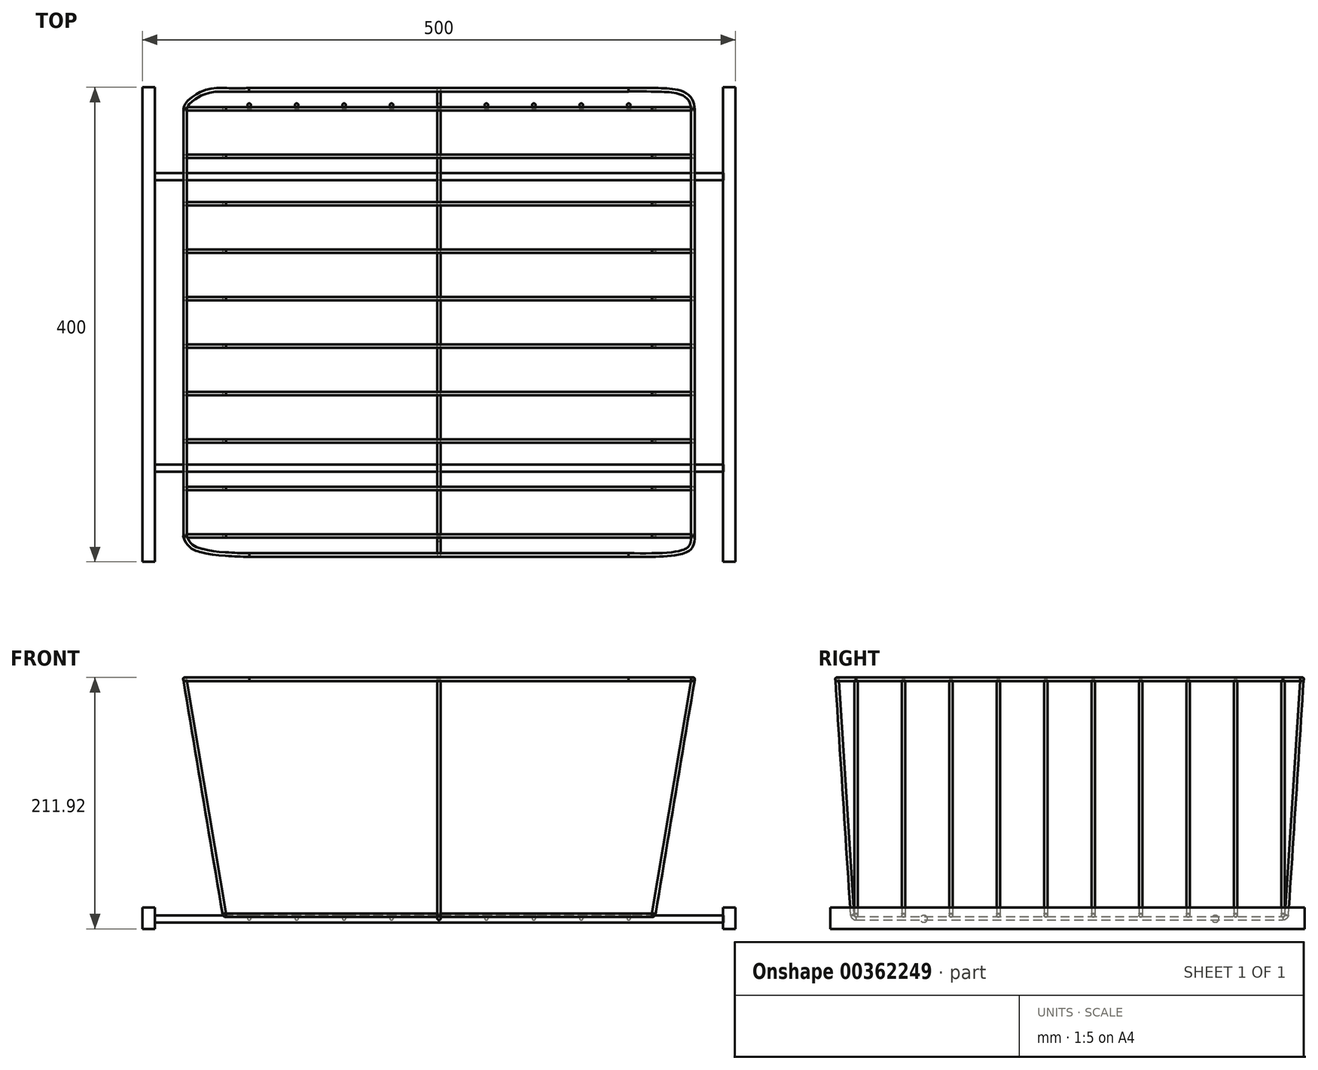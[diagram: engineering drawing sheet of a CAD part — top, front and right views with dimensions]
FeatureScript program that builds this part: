
annotation { "Feature Type Name" : "Feature", "Feature Type Description" : "" }
export const myFeature = defineFeature(function(context is Context, id is Id, definition is map)
    precondition{}
    {
        {
            var Q0;
            Q0=qCreatedBy(makeId("Front.planeOp"),FACE);
            var sketch = newSketch(context, id + "F0", { "sketchPlane" : qUnion([Q0])});
            skLineSegment(sketch, "E0.bottom", {"start": v(-179.58, 0) * mm, "end": v(180.42, 0) * mm});
            skLineSegment(sketch, "E0.top", {"start": v(-179.58, -1.5) * mm, "end": v(180.42, -1.5) * mm});
            skLineSegment(sketch, "E0.left", {"start": v(-179.58, 0) * mm, "end": v(-179.58, -1.5) * mm});
            skLineSegment(sketch, "E0.right", {"start": v(180.42, 0) * mm, "end": v(180.42, -1.5) * mm});
            skSolve(sketch);
        }
        {
            var Q0;
            Q0=makeQuery(id+"F0.imprint","IMPRINT",FACE,{"disambiguationData":[TD([[makeQuery(id+"F0.imprint","IMPRINT",EDGE,{"derivedFrom":sQuery(id+"F0.wireOp",EDGE,"E0.bottom")}),-1.0]])]});
            var Q1;
            Q1=sQuery(id+"F0.wireOp",EDGE,"E0.bottom");
            revolve(context, id + "F1", {"entities" : qUnion([Q0]), "axis" : qUnion([Q1]), "revolveType" : RevolveType.FULL});
        }
        {
            var Q0;
            Q0=qCreatedBy(makeId("Front.planeOp"),FACE);
            var sketch = newSketch(context, id + "F2", { "sketchPlane" : qUnion([Q0])});
            skLineSegment(sketch, "E1", {"start": v(-179.62, 1.46) * mm, "end": v(-212.66, 198.71) * mm});
            skLineSegment(sketch, "E2", {"start": v(-212.66, 198.71) * mm, "end": v(-214.16, 198.71) * mm});
            skLineSegment(sketch, "E3", {"start": v(-181.12, 1.46) * mm, "end": v(-179.62, 1.46) * mm});
            skLineSegment(sketch, "E4", {"start": v(-181.12, 1.46) * mm, "end": v(-214.16, 198.71) * mm});
            skSolve(sketch);
        }
        {
            var Q0;
            Q0 = qSketchRegion(id + "F2", true);
            var Q1;
            Q1=sQuery(id+"F2.wireOp",EDGE,"E4");
            revolve(context, id + "F3", {"entities" : qUnion([Q0]), "axis" : qUnion([Q1]), "revolveType" : RevolveType.FULL});
        }
        {
            var Q0;
            Q0=qCreatedBy(makeId("Front.planeOp"),FACE);
            var sketch = newSketch(context, id + "F4", { "sketchPlane" : qUnion([Q0])});
            skFitSpline(sketch, "E5", {"points": [v(-182.54, 1) * mm, v(-182.18, 0.12) * mm, v(-180.93, -1.14) * mm, v(-179.6, -1.47) * mm], "startDerivative": vector(0.9, -2.93) * mm, "endDerivative": vector(4, -0.37) * mm});
            skSolve(sketch);
        }
        {
            var Q0;
            Q0=makeQuery(id+"F1.opRevolve","SWEPT_FACE",FACE,{"disambiguationData":[OSD([sQuery(id+"F0.wireOp",EDGE,"E0.left")])]});
            var Q1;
            Q1=sQuery(id+"F4.wireOp",EDGE,"E5");
            sweep(context, id + "F5", {"profiles" : qUnion([Q0]), "path" : qUnion([Q1])});
        }
        {
            var Q0;
            Q0=makeQuery(id+"F3.opRevolve","SWEPT_BODY",BODY,{"disambiguationData":[OSD([sQuery(id+"F2.wireOp",EDGE,"E1"),sQuery(id+"F2.wireOp",EDGE,"E2"),sQuery(id+"F2.wireOp",EDGE,"E3"),sQuery(id+"F2.wireOp",EDGE,"E4")])]});
            var Q1;
            Q1=makeQuery(id+"F5.opSweep","SWEPT_BODY",BODY,{"disambiguationData":[OSD([sQuery(id+"F0.wireOp",EDGE,"E0.left"),sQuery(id+"F4.wireOp",EDGE,"E5")])]});
            var Q2;
            Q2=qCreatedBy(makeId("Right.planeOp"),FACE);
            mirror(context, id + "F6", {"operationType" : NewBodyOperationType.ADD, "entities" : qUnion([Q0, Q1]), "mirrorPlane" : qUnion([Q2])});
        }
        {
            var Q0;
            Q0=makeQuery(id+"F1.opRevolve","SWEPT_BODY",BODY,{"disambiguationData":[OSD([sQuery(id+"F0.wireOp",EDGE,"E0.bottom"),sQuery(id+"F0.wireOp",EDGE,"E0.top"),sQuery(id+"F0.wireOp",EDGE,"E0.left"),sQuery(id+"F0.wireOp",EDGE,"E0.right")])]});
            transform(context, id + "F7", {"entities" : qUnion([Q0]), "transformType" : TransformType.TRANSLATION_3D, "dx" : 0 * mm, "dy" : 40 * mm, "dz" : 0 * mm, "makeCopy" : true});
        }
        {
            var Q0;
            Q0=makeQuery(id+"F7.opPattern","COPY",BODY,{"derivedFrom":makeQuery(id+"F1.opRevolve","SWEPT_BODY",BODY,{"disambiguationData":[OSD([sQuery(id+"F0.wireOp",EDGE,"E0.bottom"),sQuery(id+"F0.wireOp",EDGE,"E0.top"),sQuery(id+"F0.wireOp",EDGE,"E0.left"),sQuery(id+"F0.wireOp",EDGE,"E0.right")])]}),"instanceName":"1"});
            transform(context, id + "F8", {"entities" : qUnion([Q0]), "transformType" : TransformType.TRANSLATION_3D, "dx" : 0 * mm, "dy" : 40 * mm, "dz" : 0 * mm, "makeCopy" : true});
        }
        {
            var Q0;
            Q0=makeQuery(id+"F8.opPattern","COPY",BODY,{"derivedFrom":makeQuery(id+"F7.opPattern","COPY",BODY,{"derivedFrom":makeQuery(id+"F1.opRevolve","SWEPT_BODY",BODY,{"disambiguationData":[OSD([sQuery(id+"F0.wireOp",EDGE,"E0.bottom"),sQuery(id+"F0.wireOp",EDGE,"E0.top"),sQuery(id+"F0.wireOp",EDGE,"E0.left"),sQuery(id+"F0.wireOp",EDGE,"E0.right")])]}),"instanceName":"1"}),"instanceName":"1"});
            transform(context, id + "F9", {"entities" : qUnion([Q0]), "transformType" : TransformType.TRANSLATION_3D, "dx" : 0 * mm, "dy" : 40 * mm, "dz" : 0 * mm, "makeCopy" : true});
        }
        {
            var Q0;
            Q0=makeQuery(id+"F9.opPattern","COPY",BODY,{"derivedFrom":makeQuery(id+"F8.opPattern","COPY",BODY,{"derivedFrom":makeQuery(id+"F7.opPattern","COPY",BODY,{"derivedFrom":makeQuery(id+"F1.opRevolve","SWEPT_BODY",BODY,{"disambiguationData":[OSD([sQuery(id+"F0.wireOp",EDGE,"E0.bottom"),sQuery(id+"F0.wireOp",EDGE,"E0.top"),sQuery(id+"F0.wireOp",EDGE,"E0.left"),sQuery(id+"F0.wireOp",EDGE,"E0.right")])]}),"instanceName":"1"}),"instanceName":"1"}),"instanceName":"1"});
            transform(context, id + "F10", {"entities" : qUnion([Q0]), "transformType" : TransformType.TRANSLATION_3D, "dx" : 0 * mm, "dy" : 40 * mm, "dz" : 0 * mm, "makeCopy" : true});
        }
        {
            var Q0;
            Q0=makeQuery(id+"F10.opPattern","COPY",BODY,{"derivedFrom":makeQuery(id+"F9.opPattern","COPY",BODY,{"derivedFrom":makeQuery(id+"F8.opPattern","COPY",BODY,{"derivedFrom":makeQuery(id+"F7.opPattern","COPY",BODY,{"derivedFrom":makeQuery(id+"F1.opRevolve","SWEPT_BODY",BODY,{"disambiguationData":[OSD([sQuery(id+"F0.wireOp",EDGE,"E0.bottom"),sQuery(id+"F0.wireOp",EDGE,"E0.top"),sQuery(id+"F0.wireOp",EDGE,"E0.left"),sQuery(id+"F0.wireOp",EDGE,"E0.right")])]}),"instanceName":"1"}),"instanceName":"1"}),"instanceName":"1"}),"instanceName":"1"});
            transform(context, id + "F11", {"entities" : qUnion([Q0]), "transformType" : TransformType.TRANSLATION_3D, "dx" : 0 * mm, "dy" : 40 * mm, "dz" : 0 * mm, "makeCopy" : true});
        }
        {
            var Q0;
            Q0=makeQuery(id+"F11.opPattern","COPY",BODY,{"derivedFrom":makeQuery(id+"F10.opPattern","COPY",BODY,{"derivedFrom":makeQuery(id+"F9.opPattern","COPY",BODY,{"derivedFrom":makeQuery(id+"F8.opPattern","COPY",BODY,{"derivedFrom":makeQuery(id+"F7.opPattern","COPY",BODY,{"derivedFrom":makeQuery(id+"F1.opRevolve","SWEPT_BODY",BODY,{"disambiguationData":[OSD([sQuery(id+"F0.wireOp",EDGE,"E0.bottom"),sQuery(id+"F0.wireOp",EDGE,"E0.top"),sQuery(id+"F0.wireOp",EDGE,"E0.left"),sQuery(id+"F0.wireOp",EDGE,"E0.right")])]}),"instanceName":"1"}),"instanceName":"1"}),"instanceName":"1"}),"instanceName":"1"}),"instanceName":"1"});
            transform(context, id + "F12", {"entities" : qUnion([Q0]), "transformType" : TransformType.TRANSLATION_3D, "dx" : 0 * mm, "dy" : 40 * mm, "dz" : 0 * mm, "makeCopy" : true});
        }
        {
            var Q0;
            Q0=makeQuery(id+"F12.opPattern","COPY",BODY,{"derivedFrom":makeQuery(id+"F11.opPattern","COPY",BODY,{"derivedFrom":makeQuery(id+"F10.opPattern","COPY",BODY,{"derivedFrom":makeQuery(id+"F9.opPattern","COPY",BODY,{"derivedFrom":makeQuery(id+"F8.opPattern","COPY",BODY,{"derivedFrom":makeQuery(id+"F7.opPattern","COPY",BODY,{"derivedFrom":makeQuery(id+"F1.opRevolve","SWEPT_BODY",BODY,{"disambiguationData":[OSD([sQuery(id+"F0.wireOp",EDGE,"E0.bottom"),sQuery(id+"F0.wireOp",EDGE,"E0.top"),sQuery(id+"F0.wireOp",EDGE,"E0.left"),sQuery(id+"F0.wireOp",EDGE,"E0.right")])]}),"instanceName":"1"}),"instanceName":"1"}),"instanceName":"1"}),"instanceName":"1"}),"instanceName":"1"}),"instanceName":"1"});
            transform(context, id + "F13", {"entities" : qUnion([Q0]), "transformType" : TransformType.TRANSLATION_3D, "dx" : 0 * mm, "dy" : 40 * mm, "dz" : 0 * mm, "makeCopy" : true});
        }
        {
            var Q0;
            Q0=makeQuery(id+"F13.opPattern","COPY",BODY,{"derivedFrom":makeQuery(id+"F12.opPattern","COPY",BODY,{"derivedFrom":makeQuery(id+"F11.opPattern","COPY",BODY,{"derivedFrom":makeQuery(id+"F10.opPattern","COPY",BODY,{"derivedFrom":makeQuery(id+"F9.opPattern","COPY",BODY,{"derivedFrom":makeQuery(id+"F8.opPattern","COPY",BODY,{"derivedFrom":makeQuery(id+"F7.opPattern","COPY",BODY,{"derivedFrom":makeQuery(id+"F1.opRevolve","SWEPT_BODY",BODY,{"disambiguationData":[OSD([sQuery(id+"F0.wireOp",EDGE,"E0.bottom"),sQuery(id+"F0.wireOp",EDGE,"E0.top"),sQuery(id+"F0.wireOp",EDGE,"E0.left"),sQuery(id+"F0.wireOp",EDGE,"E0.right")])]}),"instanceName":"1"}),"instanceName":"1"}),"instanceName":"1"}),"instanceName":"1"}),"instanceName":"1"}),"instanceName":"1"}),"instanceName":"1"});
            transform(context, id + "F14", {"entities" : qUnion([Q0]), "transformType" : TransformType.TRANSLATION_3D, "dx" : 0 * mm, "dy" : 40 * mm, "dz" : 0 * mm, "makeCopy" : true});
        }
        {
            var Q0;
            Q0=makeQuery(id+"F14.opPattern","COPY",BODY,{"derivedFrom":makeQuery(id+"F13.opPattern","COPY",BODY,{"derivedFrom":makeQuery(id+"F12.opPattern","COPY",BODY,{"derivedFrom":makeQuery(id+"F11.opPattern","COPY",BODY,{"derivedFrom":makeQuery(id+"F10.opPattern","COPY",BODY,{"derivedFrom":makeQuery(id+"F9.opPattern","COPY",BODY,{"derivedFrom":makeQuery(id+"F8.opPattern","COPY",BODY,{"derivedFrom":makeQuery(id+"F7.opPattern","COPY",BODY,{"derivedFrom":makeQuery(id+"F1.opRevolve","SWEPT_BODY",BODY,{"disambiguationData":[OSD([sQuery(id+"F0.wireOp",EDGE,"E0.bottom"),sQuery(id+"F0.wireOp",EDGE,"E0.top"),sQuery(id+"F0.wireOp",EDGE,"E0.left"),sQuery(id+"F0.wireOp",EDGE,"E0.right")])]}),"instanceName":"1"}),"instanceName":"1"}),"instanceName":"1"}),"instanceName":"1"}),"instanceName":"1"}),"instanceName":"1"}),"instanceName":"1"}),"instanceName":"1"});
            transform(context, id + "F15", {"entities" : qUnion([Q0]), "transformType" : TransformType.TRANSLATION_3D, "dx" : 0 * mm, "dy" : 40 * mm, "dz" : 0 * mm, "makeCopy" : true});
        }
        {
            var Q0;
            Q0=qCreatedBy(makeId("Right.planeOp"),FACE);
            var sketch = newSketch(context, id + "F16", { "sketchPlane" : qUnion([Q0])});
            skLineSegment(sketch, "E6.bottom", {"start": v(360, -1.07) * mm, "end": v(0, -1.07) * mm});
            skLineSegment(sketch, "E6.top", {"start": v(360, -2.57) * mm, "end": v(0, -2.57) * mm});
            skLineSegment(sketch, "E6.left", {"start": v(360, -1.07) * mm, "end": v(360, -2.57) * mm});
            skLineSegment(sketch, "E6.right", {"start": v(0, -1.07) * mm, "end": v(0, -2.57) * mm});
            skSolve(sketch);
        }
        {
            var Q0;
            Q0 = qSketchRegion(id + "F16", true);
            var Q1;
            Q1=sQuery(id+"F16.wireOp",EDGE,"E6.top");
            revolve(context, id + "F17", {"entities" : qUnion([Q0]), "axis" : qUnion([Q1]), "revolveType" : RevolveType.FULL});
        }
        {
            var Q0;
            Q0=qCreatedBy(makeId("Right.planeOp"),FACE);
            var sketch = newSketch(context, id + "F18", { "sketchPlane" : qUnion([Q0])});
            skLineSegment(sketch, "E7", {"start": v(-1.6, 0) * mm, "end": v(-14.52, 199.58) * mm});
            skLineSegment(sketch, "E8", {"start": v(-14.52, 199.58) * mm, "end": v(-16.02, 199.58) * mm});
            skLineSegment(sketch, "E9", {"start": v(-16.02, 199.58) * mm, "end": v(-3.1, 0) * mm});
            skLineSegment(sketch, "E10", {"start": v(-3.1, 0) * mm, "end": v(-1.6, 0) * mm});
            skSolve(sketch);
        }
        {
            var Q0;
            Q0 = qSketchRegion(id + "F18", true);
            var Q1;
            Q1=sQuery(id+"F18.wireOp",EDGE,"E9");
            revolve(context, id + "F19", {"entities" : qUnion([Q0]), "axis" : qUnion([Q1]), "revolveType" : RevolveType.FULL});
        }
        {
            var Q0;
            Q0=qCreatedBy(makeId("Right.planeOp"),FACE);
            var sketch = newSketch(context, id + "F20", { "sketchPlane" : qUnion([Q0])});
            skFitSpline(sketch, "E11", {"points": [v(-4.59, -0.18) * mm, v(-3.92, -1.73) * mm, v(-1.93, -3.55) * mm, v(0, -4.03) * mm], "startDerivative": vector(1.58, -5.04) * mm, "endDerivative": vector(5.92, -0.67) * mm});
            skSolve(sketch);
        }
        {
            var Q0;
            Q0=makeQuery(id+"F17.opRevolve","SWEPT_FACE",FACE,{"disambiguationData":[OSD([sQuery(id+"F16.wireOp",EDGE,"E6.right")])]});
            var Q1;
            Q1=sQuery(id+"F20.wireOp",EDGE,"E11");
            sweep(context, id + "F21", {"profiles" : qUnion([Q0]), "path" : qUnion([Q1])});
        }
        {
            var Q0;
            Q0=qCreatedBy(makeId("Front.planeOp"),FACE);
            cPlane(context, id + "F22", {"entities" : qUnion([Q0]), "cplaneType" : CPlaneType.OFFSET, "offset" : 180 * mm, "oppositeDirection" : true, "width" : 150 * mm, "height" : 150 * mm});
        }
        {
            var Q0;
            Q0=makeQuery(id+"F19.opRevolve","SWEPT_BODY",BODY,{"disambiguationData":[OSD([sQuery(id+"F18.wireOp",EDGE,"E7"),sQuery(id+"F18.wireOp",EDGE,"E8"),sQuery(id+"F18.wireOp",EDGE,"E9"),sQuery(id+"F18.wireOp",EDGE,"E10")])]});
            var Q1;
            Q1=makeQuery(id+"F21.opSweep","SWEPT_BODY",BODY,{"disambiguationData":[OSD([sQuery(id+"F16.wireOp",EDGE,"E6.right"),sQuery(id+"F20.wireOp",EDGE,"E11")])]});
            var Q2;
            Q2=qCreatedBy(id+"F22.planeOp",FACE);
            mirror(context, id + "F23", {"entities" : qUnion([Q0, Q1]), "mirrorPlane" : qUnion([Q2])});
        }
        {
            var Q0;
            Q0=makeQuery(id+"F23.opPattern","COPY",BODY,{"derivedFrom":makeQuery(id+"F21.opSweep","SWEPT_BODY",BODY,{"disambiguationData":[OSD([sQuery(id+"F16.wireOp",EDGE,"E6.right"),sQuery(id+"F20.wireOp",EDGE,"E11")])]}),"instanceName":"1"});
            transform(context, id + "F24", {"entities" : qUnion([Q0]), "transformType" : TransformType.TRANSLATION_3D, "dx" : 40 * mm, "dy" : 0 * mm, "dz" : 0 * mm, "makeCopy" : true});
        }
        {
            var Q0;
            Q0=makeQuery(id+"F24.opPattern","COPY",BODY,{"derivedFrom":makeQuery(id+"F23.opPattern","COPY",BODY,{"derivedFrom":makeQuery(id+"F21.opSweep","SWEPT_BODY",BODY,{"disambiguationData":[OSD([sQuery(id+"F16.wireOp",EDGE,"E6.right"),sQuery(id+"F20.wireOp",EDGE,"E11")])]}),"instanceName":"1"}),"instanceName":"1"});
            transform(context, id + "F25", {"entities" : qUnion([Q0]), "transformType" : TransformType.TRANSLATION_3D, "dx" : 40 * mm, "dy" : 0 * mm, "dz" : 0 * mm, "makeCopy" : true});
        }
        {
            var Q0;
            Q0=makeQuery(id+"F25.opPattern","COPY",BODY,{"derivedFrom":makeQuery(id+"F24.opPattern","COPY",BODY,{"derivedFrom":makeQuery(id+"F23.opPattern","COPY",BODY,{"derivedFrom":makeQuery(id+"F21.opSweep","SWEPT_BODY",BODY,{"disambiguationData":[OSD([sQuery(id+"F16.wireOp",EDGE,"E6.right"),sQuery(id+"F20.wireOp",EDGE,"E11")])]}),"instanceName":"1"}),"instanceName":"1"}),"instanceName":"1"});
            transform(context, id + "F26", {"entities" : qUnion([Q0]), "transformType" : TransformType.TRANSLATION_3D, "dx" : 40 * mm, "dy" : 0 * mm, "dz" : 0 * mm, "makeCopy" : true});
        }
        {
            var Q0;
            Q0=makeQuery(id+"F26.opPattern","COPY",BODY,{"derivedFrom":makeQuery(id+"F25.opPattern","COPY",BODY,{"derivedFrom":makeQuery(id+"F24.opPattern","COPY",BODY,{"derivedFrom":makeQuery(id+"F23.opPattern","COPY",BODY,{"derivedFrom":makeQuery(id+"F21.opSweep","SWEPT_BODY",BODY,{"disambiguationData":[OSD([sQuery(id+"F16.wireOp",EDGE,"E6.right"),sQuery(id+"F20.wireOp",EDGE,"E11")])]}),"instanceName":"1"}),"instanceName":"1"}),"instanceName":"1"}),"instanceName":"1"});
            transform(context, id + "F27", {"entities" : qUnion([Q0]), "transformType" : TransformType.TRANSLATION_3D, "dx" : 40 * mm, "dy" : 0 * mm, "dz" : 0 * mm, "makeCopy" : true});
        }
        {
            var Q0;
            Q0=makeQuery(id+"F23.opPattern","COPY",BODY,{"derivedFrom":makeQuery(id+"F21.opSweep","SWEPT_BODY",BODY,{"disambiguationData":[OSD([sQuery(id+"F16.wireOp",EDGE,"E6.right"),sQuery(id+"F20.wireOp",EDGE,"E11")])]}),"instanceName":"1"});
            transform(context, id + "F28", {"entities" : qUnion([Q0]), "transformType" : TransformType.TRANSLATION_3D, "dx" : -40 * mm, "dy" : 0 * mm, "dz" : 0 * mm, "makeCopy" : true});
        }
        {
            var Q0;
            Q0=makeQuery(id+"F28.opPattern","COPY",BODY,{"derivedFrom":makeQuery(id+"F23.opPattern","COPY",BODY,{"derivedFrom":makeQuery(id+"F21.opSweep","SWEPT_BODY",BODY,{"disambiguationData":[OSD([sQuery(id+"F16.wireOp",EDGE,"E6.right"),sQuery(id+"F20.wireOp",EDGE,"E11")])]}),"instanceName":"1"}),"instanceName":"1"});
            transform(context, id + "F29", {"entities" : qUnion([Q0]), "transformType" : TransformType.TRANSLATION_3D, "dx" : -40 * mm, "dy" : 0 * mm, "dz" : 0 * mm, "makeCopy" : true});
        }
        {
            var Q0;
            Q0=makeQuery(id+"F29.opPattern","COPY",BODY,{"derivedFrom":makeQuery(id+"F28.opPattern","COPY",BODY,{"derivedFrom":makeQuery(id+"F23.opPattern","COPY",BODY,{"derivedFrom":makeQuery(id+"F21.opSweep","SWEPT_BODY",BODY,{"disambiguationData":[OSD([sQuery(id+"F16.wireOp",EDGE,"E6.right"),sQuery(id+"F20.wireOp",EDGE,"E11")])]}),"instanceName":"1"}),"instanceName":"1"}),"instanceName":"1"});
            transform(context, id + "F30", {"entities" : qUnion([Q0]), "transformType" : TransformType.TRANSLATION_3D, "dx" : -40 * mm, "dy" : 0 * mm, "dz" : 0 * mm, "makeCopy" : true});
        }
        {
            var Q0;
            Q0=makeQuery(id+"F30.opPattern","COPY",BODY,{"derivedFrom":makeQuery(id+"F29.opPattern","COPY",BODY,{"derivedFrom":makeQuery(id+"F28.opPattern","COPY",BODY,{"derivedFrom":makeQuery(id+"F23.opPattern","COPY",BODY,{"derivedFrom":makeQuery(id+"F21.opSweep","SWEPT_BODY",BODY,{"disambiguationData":[OSD([sQuery(id+"F16.wireOp",EDGE,"E6.right"),sQuery(id+"F20.wireOp",EDGE,"E11")])]}),"instanceName":"1"}),"instanceName":"1"}),"instanceName":"1"}),"instanceName":"1"});
            transform(context, id + "F31", {"entities" : qUnion([Q0]), "transformType" : TransformType.TRANSLATION_3D, "dx" : -40 * mm, "dy" : 0 * mm, "dz" : 0 * mm, "makeCopy" : true});
        }
        {
            var Q0;
            Q0=qCreatedBy(makeId("Top.planeOp"),FACE);
            cPlane(context, id + "F32", {"entities" : qUnion([Q0]), "cplaneType" : CPlaneType.OFFSET, "offset" : 199 * mm, "width" : 150 * mm, "height" : 150 * mm});
        }
        {
            var Q0;
            Q0=qCreatedBy(id+"F32.planeOp",FACE);
            var sketch = newSketch(context, id + "F33", { "sketchPlane" : qUnion([Q0])});
            skLineSegment(sketch, "E12.bottom", {"start": v(-160.03, -16.04) * mm, "end": v(159.97, -16.04) * mm});
            skLineSegment(sketch, "E12.top", {"start": v(-160.03, -17.54) * mm, "end": v(159.97, -17.54) * mm});
            skLineSegment(sketch, "E12.left", {"start": v(-160.03, -16.04) * mm, "end": v(-160.03, -17.54) * mm});
            skLineSegment(sketch, "E12.right", {"start": v(159.97, -16.04) * mm, "end": v(159.97, -17.54) * mm});
            skSolve(sketch);
        }
        {
            var Q0;
            Q0=makeQuery(id+"F33.imprint","IMPRINT",FACE,{"disambiguationData":[TD([[makeQuery(id+"F33.imprint","IMPRINT",EDGE,{"derivedFrom":sQuery(id+"F33.wireOp",EDGE,"E12.bottom")}),-1.0]])]});
            var Q1;
            Q1=sQuery(id+"F33.wireOp",EDGE,"E12.bottom");
            revolve(context, id + "F34", {"entities" : qUnion([Q0]), "axis" : qUnion([Q1]), "revolveType" : RevolveType.FULL});
        }
        {
            var Q0;
            Q0=qCreatedBy(id+"F32.planeOp",FACE);
            var sketch = newSketch(context, id + "F35", { "sketchPlane" : qUnion([Q0])});
            skLineSegment(sketch, "E13.bottom", {"start": v(-160.06, 376.04) * mm, "end": v(159.94, 376.04) * mm});
            skLineSegment(sketch, "E13.top", {"start": v(-160.06, 377.54) * mm, "end": v(159.94, 377.54) * mm});
            skLineSegment(sketch, "E13.left", {"start": v(-160.06, 376.04) * mm, "end": v(-160.06, 377.54) * mm});
            skLineSegment(sketch, "E13.right", {"start": v(159.94, 376.04) * mm, "end": v(159.94, 377.54) * mm});
            skSolve(sketch);
        }
        {
            var Q0;
            Q0 = qSketchRegion(id + "F35", true);
            var Q1;
            Q1=sQuery(id+"F35.wireOp",EDGE,"E13.bottom");
            revolve(context, id + "F36", {"entities" : qUnion([Q0]), "axis" : qUnion([Q1]), "revolveType" : RevolveType.FULL});
        }
        {
            var Q0;
            Q0=qCreatedBy(id+"F32.planeOp",FACE);
            var sketch = newSketch(context, id + "F37", { "sketchPlane" : qUnion([Q0])});
            skLineSegment(sketch, "E14.bottom", {"start": v(-215.6, 360) * mm, "end": v(-214.1, 360) * mm});
            skLineSegment(sketch, "E14.top", {"start": v(-215.6, 0) * mm, "end": v(-214.1, 0) * mm});
            skLineSegment(sketch, "E14.left", {"start": v(-215.6, 360) * mm, "end": v(-215.6, 0) * mm});
            skLineSegment(sketch, "E14.right", {"start": v(-214.1, 360) * mm, "end": v(-214.1, 0) * mm});
            skSolve(sketch);
        }
        {
            var Q0;
            Q0 = qSketchRegion(id + "F37", true);
            var Q1;
            Q1=sQuery(id+"F37.wireOp",EDGE,"E14.right");
            revolve(context, id + "F38", {"entities" : qUnion([Q0]), "axis" : qUnion([Q1]), "revolveType" : RevolveType.FULL});
        }
        {
            var Q0;
            Q0=qCreatedBy(id+"F32.planeOp",FACE);
            var sketch = newSketch(context, id + "F39", { "sketchPlane" : qUnion([Q0])});
            skFitSpline(sketch, "E15", {"points": [v(-215.61, 0) * mm, v(-201.65, -13.22) * mm, v(-185.72, -16.08) * mm, v(-159.95, -17.32) * mm], "startDerivative": vector(28.9, -88.62) * mm, "endDerivative": vector(69.27, -0.56) * mm});
            skSolve(sketch);
        }
        {
            var Q0;
            Q0=makeQuery(id+"F34.opRevolve","SWEPT_FACE",FACE,{"disambiguationData":[OSD([sQuery(id+"F33.wireOp",EDGE,"E12.left")])]});
            var Q1;
            Q1=sQuery(id+"F39.wireOp",EDGE,"E15");
            sweep(context, id + "F40", {"profiles" : qUnion([Q0]), "path" : qUnion([Q1])});
        }
        {
            var Q0;
            Q0=qCreatedBy(id+"F32.planeOp",FACE);
            var sketch = newSketch(context, id + "F41", { "sketchPlane" : qUnion([Q0])});
            skFitSpline(sketch, "E16", {"points": [v(-160.14, 377.49) * mm, v(-177.98, 377.45) * mm, v(-198.2, 375.36) * mm, v(-215.39, 360.13) * mm], "startDerivative": vector(-59.47, -0.43) * mm, "endDerivative": vector(-3.54, -51.4) * mm});
            skSolve(sketch);
        }
        {
            var Q0;
            Q0=makeQuery(id+"F36.opRevolve","SWEPT_FACE",FACE,{"disambiguationData":[OSD([sQuery(id+"F35.wireOp",EDGE,"E13.left")])]});
            var Q1;
            Q1=sQuery(id+"F41.wireOp",EDGE,"E16");
            sweep(context, id + "F42", {"profiles" : qUnion([Q0]), "path" : qUnion([Q1])});
        }
        {
            var Q0;
            Q0=qCreatedBy(id+"F32.planeOp",FACE);
            var sketch = newSketch(context, id + "F43", { "sketchPlane" : qUnion([Q0])});
            skLineSegment(sketch, "E17.bottom", {"start": v(214.08, 360) * mm, "end": v(215.58, 360) * mm});
            skLineSegment(sketch, "E17.top", {"start": v(214.08, 0) * mm, "end": v(215.58, 0) * mm});
            skLineSegment(sketch, "E17.left", {"start": v(214.08, 360) * mm, "end": v(214.08, 0) * mm});
            skLineSegment(sketch, "E17.right", {"start": v(215.58, 360) * mm, "end": v(215.58, 0) * mm});
            skSolve(sketch);
        }
        {
            var Q0;
            Q0 = qSketchRegion(id + "F43", true);
            var Q1;
            Q1=sQuery(id+"F43.wireOp",EDGE,"E17.left");
            revolve(context, id + "F44", {"entities" : qUnion([Q0]), "axis" : qUnion([Q1]), "revolveType" : RevolveType.FULL});
        }
        {
            var Q0;
            Q0=qCreatedBy(id+"F32.planeOp",FACE);
            var sketch = newSketch(context, id + "F45", { "sketchPlane" : qUnion([Q0])});
            skFitSpline(sketch, "E18", {"points": [v(159.86, -17.3) * mm, v(193.94, -16.7) * mm, v(210.75, -12.31) * mm, v(215.54, 0) * mm], "startDerivative": vector(59.2, -0.2) * mm, "endDerivative": vector(3.02, 82.73) * mm});
            skSolve(sketch);
        }
        {
            var Q0;
            Q0=makeQuery(id+"F34.opRevolve","SWEPT_FACE",FACE,{"disambiguationData":[OSD([sQuery(id+"F33.wireOp",EDGE,"E12.right")])]});
            var Q1;
            Q1=sQuery(id+"F45.wireOp",EDGE,"E18");
            sweep(context, id + "F46", {"profiles" : qUnion([Q0]), "path" : qUnion([Q1])});
        }
        {
            var Q0;
            Q0=qCreatedBy(id+"F32.planeOp",FACE);
            var sketch = newSketch(context, id + "F47", { "sketchPlane" : qUnion([Q0])});
            skFitSpline(sketch, "E19", {"points": [v(159.76, 377.64) * mm, v(188.68, 377.38) * mm, v(206.7, 374.17) * mm, v(215.56, 360.06) * mm], "startDerivative": vector(107.52, 0.78) * mm, "endDerivative": vector(1.64, -73.97) * mm});
            skSolve(sketch);
        }
        {
            var Q0;
            Q0=makeQuery(id+"F44.opRevolve","SWEPT_FACE",FACE,{"disambiguationData":[OSD([sQuery(id+"F43.wireOp",EDGE,"E17.bottom")])]});
            var Q1;
            Q1=sQuery(id+"F47.wireOp",EDGE,"E19");
            sweep(context, id + "F48", {"profiles" : qUnion([Q0]), "path" : qUnion([Q1])});
        }
        {
            var Q0;
            Q0=qCreatedBy(makeId("Top.planeOp"),FACE);
            cPlane(context, id + "F49", {"entities" : qUnion([Q0]), "cplaneType" : CPlaneType.OFFSET, "offset" : 3 * mm, "oppositeDirection" : true, "width" : 150 * mm, "height" : 150 * mm});
        }
        {
            var Q0;
            Q0=qCreatedBy(id+"F49.planeOp",FACE);
            var sketch = newSketch(context, id + "F50", { "sketchPlane" : qUnion([Q0])});
            skLineSegment(sketch, "E20.bottom", {"start": v(-239.66, 54.14) * mm, "end": v(240.34, 54.14) * mm});
            skLineSegment(sketch, "E20.top", {"start": v(-239.66, 57.14) * mm, "end": v(240.34, 57.14) * mm});
            skLineSegment(sketch, "E20.left", {"start": v(-239.66, 54.14) * mm, "end": v(-239.66, 57.14) * mm});
            skLineSegment(sketch, "E20.right", {"start": v(240.34, 54.14) * mm, "end": v(240.34, 57.14) * mm});
            skSolve(sketch);
        }
        {
            var Q0;
            Q0 = qSketchRegion(id + "F50", true);
            var Q1;
            Q1=sQuery(id+"F50.wireOp",EDGE,"E20.top");
            revolve(context, id + "F51", {"entities" : qUnion([Q0]), "axis" : qUnion([Q1]), "revolveType" : RevolveType.FULL});
        }
        {
            var Q0;
            Q0=makeQuery(id+"F51.opRevolve","SWEPT_BODY",BODY,{"disambiguationData":[OSD([sQuery(id+"F50.wireOp",EDGE,"E20.bottom"),sQuery(id+"F50.wireOp",EDGE,"E20.top"),sQuery(id+"F50.wireOp",EDGE,"E20.left"),sQuery(id+"F50.wireOp",EDGE,"E20.right")])]});
            var Q1;
            Q1=qCreatedBy(id+"F22.planeOp",FACE);
            mirror(context, id + "F52", {"entities" : qUnion([Q0]), "mirrorPlane" : qUnion([Q1])});
        }
        {
            var Q0;
            Q0=makeQuery(id+"F52.opPattern","COPY",FACE,{"derivedFrom":makeQuery(id+"F51.opRevolve","SWEPT_FACE",FACE,{"disambiguationData":[OSD([sQuery(id+"F50.wireOp",EDGE,"E20.left")])]}),"instanceName":"1"});
            cPlane(context, id + "F53", {"entities" : qUnion([Q0]), "cplaneType" : CPlaneType.OFFSET, "offset" : 0 * mm, "width" : 150 * mm, "height" : 150 * mm});
        }
        {
            var Q0;
            Q0=qCreatedBy(id+"F53.planeOp",FACE);
            var sketch = newSketch(context, id + "F54", { "sketchPlane" : qUnion([Q0])});
            skLineSegment(sketch, "E21.bottom", {"start": v(-378.24, 6.58) * mm, "end": v(21.76, 6.58) * mm});
            skLineSegment(sketch, "E21.top", {"start": v(-378.24, -11.42) * mm, "end": v(21.76, -11.42) * mm});
            skLineSegment(sketch, "E21.left", {"start": v(-378.24, 6.58) * mm, "end": v(-378.24, -11.42) * mm});
            skLineSegment(sketch, "E21.right", {"start": v(21.76, 6.58) * mm, "end": v(21.76, -11.42) * mm});
            skSolve(sketch);
        }
        {
            var Q0;
            Q0 = qSketchRegion(id + "F54", true);
            extrude(context, id + "F55", {"entities" : qUnion([Q0]), "depth" : 10.34 * mm});
        }
        {
            var Q0;
            Q0=makeQuery(id+"F55.opExtrude","SWEPT_BODY",BODY,{"disambiguationData":[OSD([sQuery(id+"F54.wireOp",EDGE,"E21.bottom"),sQuery(id+"F54.wireOp",EDGE,"E21.top"),sQuery(id+"F54.wireOp",EDGE,"E21.left"),sQuery(id+"F54.wireOp",EDGE,"E21.right")])]});
            var Q1;
            Q1=qCreatedBy(makeId("Right.planeOp"),FACE);
            mirror(context, id + "F56", {"entities" : qUnion([Q0]), "mirrorPlane" : qUnion([Q1])});
        }
    });
